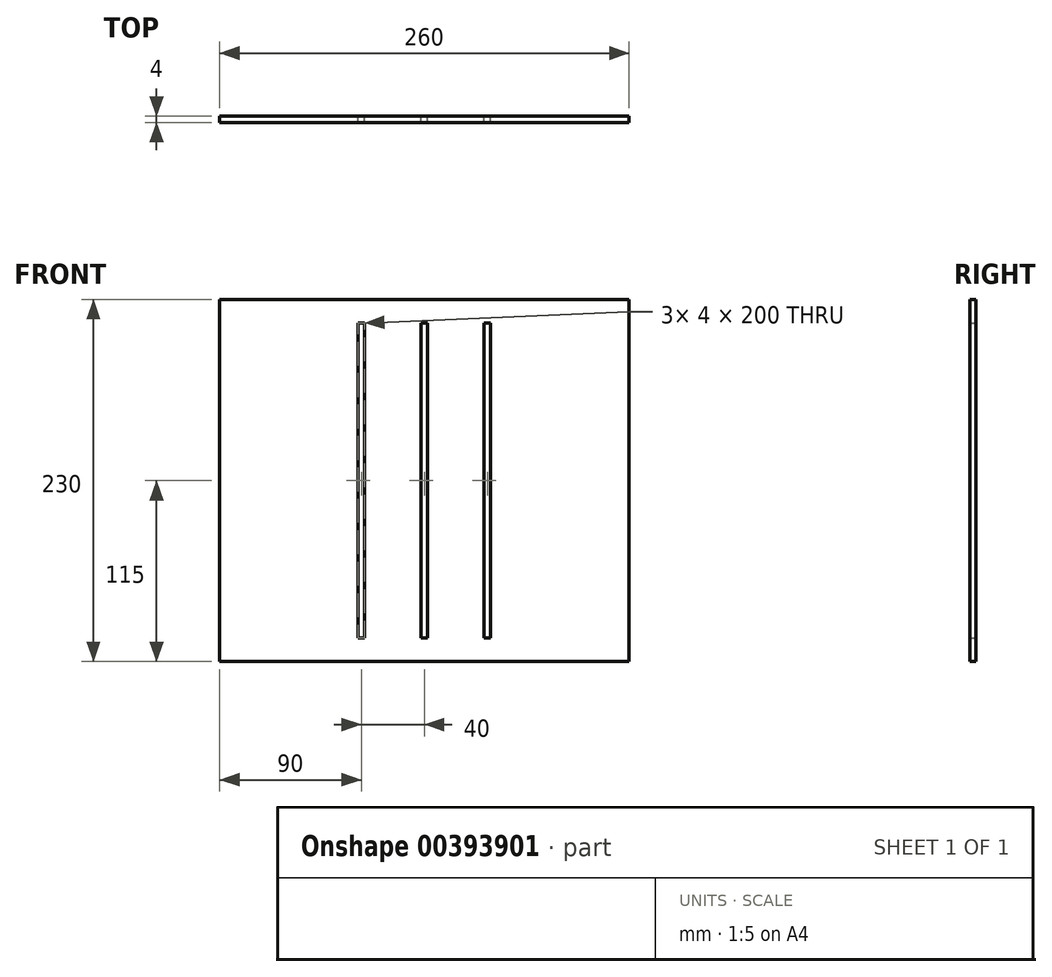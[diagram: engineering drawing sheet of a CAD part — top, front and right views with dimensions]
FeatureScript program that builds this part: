
annotation { "Feature Type Name" : "Feature", "Feature Type Description" : "" }
export const myFeature = defineFeature(function(context is Context, id is Id, definition is map)
    precondition{}
    {
        {
            var Q0;
            Q0=qCreatedBy(makeId("Front.planeOp"),FACE);
            var sketch = newSketch(context, id + "F0", { "sketchPlane" : qUnion([Q0])});
            skLineSegment(sketch, "E0.bottom", {"start": v(130, 115) * mm, "end": v(-130, 115) * mm});
            skLineSegment(sketch, "E0.top", {"start": v(130, -115) * mm, "end": v(-130, -115) * mm});
            skLineSegment(sketch, "E0.left", {"start": v(130, 115) * mm, "end": v(130, -115) * mm});
            skLineSegment(sketch, "E0.right", {"start": v(-130, 115) * mm, "end": v(-130, -115) * mm});
            skPoint(sketch, "E0.middle", {"position": v(0, 0) * mm});
            skLineSegment(sketch, "E1", {"start": v(40, 100) * mm, "end": v(-40, 100) * mm, "construction": true});
            skLineSegment(sketch, "E2.MirrorCS", {"start": v(40, -100) * mm, "end": v(-40, -100) * mm, "construction": true});
            skLineSegment(sketch, "E3.bottom", {"start": v(38, 100) * mm, "end": v(42, 100) * mm});
            skLineSegment(sketch, "E3.top", {"start": v(38, -100) * mm, "end": v(42, -100) * mm});
            skLineSegment(sketch, "E3.left", {"start": v(38, 100) * mm, "end": v(38, -100) * mm});
            skLineSegment(sketch, "E3.right", {"start": v(42, 100) * mm, "end": v(42, -100) * mm});
            skLineSegment(sketch, "E4.MirrorCS", {"start": v(-38, 100) * mm, "end": v(-38, -100) * mm});
            skLineSegment(sketch, "E5.MirrorCS", {"start": v(-42, 100) * mm, "end": v(-42, -100) * mm});
            skLineSegment(sketch, "E6.MirrorCS", {"start": v(-38, 100) * mm, "end": v(-42, 100) * mm});
            skLineSegment(sketch, "E7.MirrorCS", {"start": v(-38, -100) * mm, "end": v(-42, -100) * mm});
            skLineSegment(sketch, "E8.bottom", {"start": v(-2, 100) * mm, "end": v(2, 100) * mm});
            skLineSegment(sketch, "E8.top", {"start": v(-2, -100) * mm, "end": v(2, -100) * mm});
            skLineSegment(sketch, "E8.left", {"start": v(-2, 100) * mm, "end": v(-2, -100) * mm});
            skLineSegment(sketch, "E8.right", {"start": v(2, 100) * mm, "end": v(2, -100) * mm});
            skSolve(sketch);
        }
        {
            var Q0;
            Q0=makeQuery(id+"F0.imprint","IMPRINT",FACE,{"disambiguationData":[TD([[makeQuery(id+"F0.imprint","IMPRINT",EDGE,{"derivedFrom":sQuery(id+"F0.wireOp",EDGE,"E0.bottom")}),1.0]])]});
            extrude(context, id + "F1", {"entities" : qUnion([Q0]), "depth" : 4 * mm, "offsetDistance" : 25 * mm});
        }
    });
